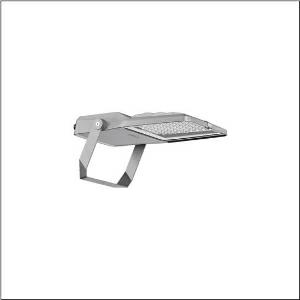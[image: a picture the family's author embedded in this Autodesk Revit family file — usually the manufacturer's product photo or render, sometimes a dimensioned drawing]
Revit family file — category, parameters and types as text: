
# Revit family: floodlight_fl_21_iq_mini___rs12_5xa7772b5b1a_54c6
name_source: partatom
category: Lighting Fixtures
units: mm (PartAtom-declared; Revit-internal decimal feet)

## family parameters
Cut with Voids When Loaded = No
Host = Face
Light Source = No
Part Type = Normal
Room Calculation Point = No
Round Connector Dimension = Use Diameter
Shared = No

## types (1)
- --- (1 x LED, 5880 lm, 45.5 W, 4000K)
    Apparent Load = 46 VA
    CIE Flux Codes = 79 92 99 100 100
    Color Rendering = 80
    Color Temperature = 4000K
    Default Elevation = 1800 mm
    Description = Floodlight FL 21 iQ mini, floodlight, primary light control with lens, of PMMA, primary optical cover: protective disc, of toughened safety glass, transparent, light distribution: RS12, light emission: direct distribution, installation type: surface-mounted, LED, High Power LED, rated luminous flux: 5.880lm, luminous efficacy: 129lm/W, light colour: 840, colour temperature: 4000K, control gear: iQ Street-Remote/DALI, control: Street-Remote, Auto-Match, Temp-Guard, Night-Set, Smart-Wire, Desk-Remote (wireless, voltage-free reading and setting of iQ features in the workshop via application-optimized NFC function/RFID function), optimised constant luminous flux control (CLO 2.0), with terminal, 6-pole, mains connection: 220..240V, AC, 50/60Hz, start of lifetime: 46W, end of service life: 48W, reduction: 22W, luminaire housing, of diecast aluminium, powder-coated, Siteco® metallic grey (DB 702S), corrosivity category C5 mid according to DIN EN ISO 12944, suitable for swimming pools, chlorine-resistant, sealing non-destructively replaceable, mounting bracket, of steel, galvanised, powder-coated, Siteco® metallic grey (DB 702S), protection rating (complete): IP66, insulation class (complete): insulation class II (safety insulation), certification: CE, ENEC, VDE, protection symbol: D, impact resistance: IK08, permissible operating ambient temperature: -40..+40°C, permissible operating ambient temperature for outdoor applications: -40..+50°C, standard: DIN EN 12944, LABS conformity tested according to VDMA 24364:2018-05, packaging unit: 1 piece

Light Distribution: RS12
    Height = 70 mm
    Lamp = 1 x LED
    Lamp Light Flux = 5880 lm
    Lamp Power = 45.5 W
    Lamp count = 1
    Length = 485 mm
    Luminous efficacy = 129 lm/W
    Manufacturer = Siteco
    ModVariant = No
    Model = 5XA7772B5B1A
    Number of Poles = 1
    OnlyDefault = Yes
    Power Factor = 1
    Product Name = Floodlight FL 21 iQ mini | RS12
    Product group = floodlight | pylon annexe
    ProductGroupID = 6200
    Protection Class = Protection class II
    Protection Degree = IP 66
    RLX_Detail_Level = 1
    RLX_Emergency_Light_Flux = 0 lm
    RLX_Emergency_Type = 0
    RLX_Emergency_Type_DB = No
    RlxData = <blob elided: 90981 chars, md5=8bf471a2>
    Socket = socket
    Standby Power = 0 W
    System Light Flux = 5880 lm
    System Power = 46 W
    Type Comments = factory setting: luminous flux: 100 % | dim-lin: 254 | 463 mA
    Type Image = l_1006845.jpg
    URL = http://relux.com
    VarID = @adj_167780
    Voltage = 0 V
    Weight = 0.00 kg
    Width = 337 mm

## geometry (parser evidence)
native form markers: Blend x4, Sweep x12
no freeform markers — native parametric forms only
